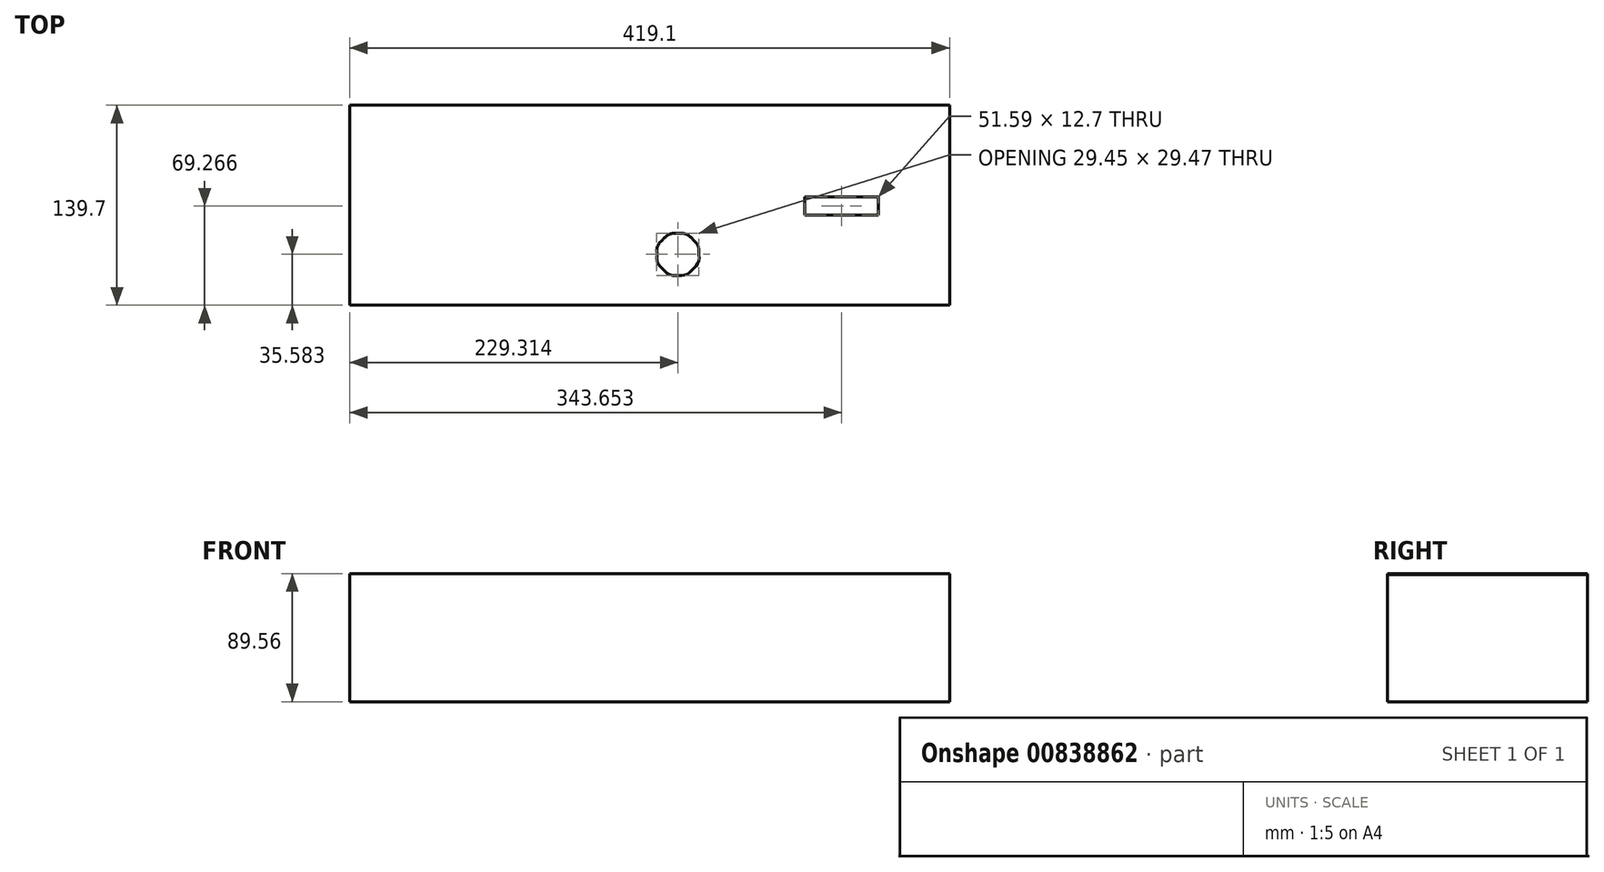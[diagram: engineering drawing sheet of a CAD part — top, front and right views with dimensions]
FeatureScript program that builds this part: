
annotation { "Feature Type Name" : "Feature", "Feature Type Description" : "" }
export const myFeature = defineFeature(function(context is Context, id is Id, definition is map)
    precondition{}
    {
        {
            var Q0;
            Q0=qCreatedBy(makeId("Right.planeOp"),FACE);
            var sketch = newSketch(context, id + "F0", { "sketchPlane" : qUnion([Q0])});
            skLineSegment(sketch, "E0.bottom", {"start": v(0, 0) * mm, "end": v(-139.7, 0) * mm});
            skLineSegment(sketch, "E0.top", {"start": v(0, 88.9) * mm, "end": v(-139.3, 88.9) * mm});
            skLineSegment(sketch, "E0.left", {"start": v(0, 0) * mm, "end": v(0, 88.9) * mm});
            skLineSegment(sketch, "E0.right", {"start": v(-139.7, 0) * mm, "end": v(-139.7, 89.56) * mm});
            skLineSegment(sketch, "E1", {"start": v(-139.7, 89.56) * mm, "end": v(0, 89.56) * mm});
            skLineSegment(sketch, "E2", {"start": v(0, 89.56) * mm, "end": v(0, 89.15) * mm});
            skLineSegment(sketch, "E3", {"start": v(0, 89.15) * mm, "end": v(-139.3, 89.15) * mm});
            skLineSegment(sketch, "E4", {"start": v(-139.3, 88.9) * mm, "end": v(-139.3, 89.15) * mm});
            skLineSegment(sketch, "E5", {"start": v(-139.3, 88.9) * mm, "end": v(-139.7, 88.9) * mm, "construction": true});
            skSolve(sketch);
        }
        {
            var Q0;
            Q0 = qSketchRegion(id + "F0", true);
            extrude(context, id + "F1", {"entities" : qUnion([Q0]), "endBound" : BoundingType.SYMMETRIC, "depth" : 419.1 * mm, "offsetDistance" : 25.4 * mm});
        }
        {
            var Q0;
            Q0=makeQuery(id+"F1.opExtrude","SWEPT_FACE",FACE,{"disambiguationData":[OSD([sQuery(id+"F0.wireOp",EDGE,"E1")])]});
            var sketch = newSketch(context, id + "F2", { "sketchPlane" : qUnion([Q0])});
            skLineSegment(sketch, "E6", {"start": v(-208.8, -140.28) * mm, "end": v(-208.8, -1.38) * mm, "construction": true});
            skLineSegment(sketch, "E7", {"start": v(108.3, -76.78) * mm, "end": v(159.9, -76.78) * mm});
            skLineSegment(sketch, "E8", {"start": v(210.3, -140.28) * mm, "end": v(210.3, -1.38) * mm, "construction": true});
            skLineSegment(sketch, "E9", {"start": v(159.9, -76.78) * mm, "end": v(159.9, -64.08) * mm});
            skLineSegment(sketch, "E10", {"start": v(159.9, -64.08) * mm, "end": v(108.3, -64.08) * mm});
            skLineSegment(sketch, "E11", {"start": v(108.3, -64.08) * mm, "end": v(108.3, -76.78) * mm});
            skLineSegment(sketch, "E12", {"start": v(-208.8, -1.38) * mm, "end": v(210.3, -1.38) * mm, "construction": true});
            skLineSegment(sketch, "E13", {"start": v(210.3, -140.28) * mm, "end": v(-208.8, -140.28) * mm, "construction": true});
            skFitSpline(sketch, "E14", {"points": [v(19.8, -89.48) * mm, v(15.96, -89.48) * mm, v(12.14, -91.07) * mm, v(9.42, -93.78) * mm]});
            skFitSpline(sketch, "E15", {"points": [v(9.42, -93.78) * mm, v(6.7, -96.5) * mm, v(5.12, -100.32) * mm, v(5.12, -104.17) * mm, v(5.12, -108.01) * mm, v(6.7, -111.83) * mm, v(9.42, -114.55) * mm]});
            skFitSpline(sketch, "E16", {"points": [v(9.42, -114.55) * mm, v(12.14, -117.27) * mm, v(15.96, -118.85) * mm, v(19.8, -118.85) * mm, v(23.65, -118.85) * mm, v(27.47, -117.27) * mm, v(30.19, -114.55) * mm, v(32.9, -111.83) * mm, v(34.49, -108.01) * mm, v(34.49, -104.17) * mm, v(34.49, -100.32) * mm, v(32.9, -96.5) * mm, v(30.19, -93.78) * mm]});
            skFitSpline(sketch, "E17", {"points": [v(30.19, -93.78) * mm, v(27.47, -91.07) * mm, v(23.65, -89.48) * mm, v(19.8, -89.48) * mm]});
            skSolve(sketch);
        }
        {
            var Q0;
            Q0 = qSketchRegion(id + "F2", true);
            var Q1;
            Q1=makeQuery(id+"F1.opExtrude","SWEPT_FACE",FACE,{"disambiguationData":[OSD([sQuery(id+"F0.wireOp",EDGE,"E3")])]});
            extrude(context, id + "F3", {"entities" : qUnion([Q0]), "operationType" : NewBodyOperationType.REMOVE, "endBound" : BoundingType.UP_TO_SURFACE, "oppositeDirection" : true, "depth" : 25.4 * mm, "endBoundEntityFace" : qUnion([Q1]), "offsetDistance" : 25.4 * mm});
        }
    });
